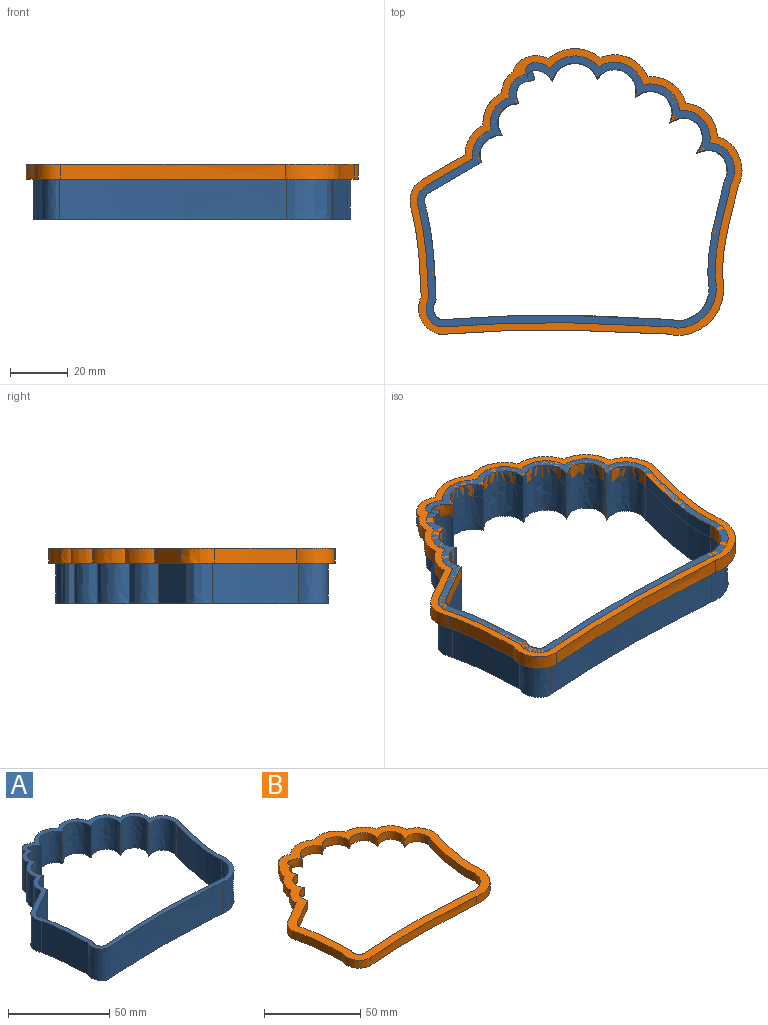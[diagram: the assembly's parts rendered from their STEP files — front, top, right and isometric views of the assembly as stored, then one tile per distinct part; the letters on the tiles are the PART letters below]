
ASSEMBLY  parts=2 mates=1
PART A: 36 faces, bbox 113.9x98.3x23.4 mm
  f0: plane 113.92x98.34mm, normal (0,0,1), area 899.7mm2, adj f2,f3,f4,f5,f6,f7,f8,f9
  f1: plane 113.92x98.34mm, normal (0,0,-1), area 899.7mm2, adj f2,f3,f4,f5,f6,f7,f8,f9
  f2: extruded ~19.05x1.86mm, area 34.7mm2, adj f0,f1,f15,f16
  f3: plane 19.05x16.29mm, normal (-0.5,0.87,0), area 358.4mm2, adj f0,f1,f4,f18
  f4: extruded ~19.05x9.03mm, area 192.8mm2, adj f0,f1,f3,f5
  f5: extruded ~29.67x19.05mm, area 569.3mm2, adj f0,f1,f4,f6
  f6: extruded ~19.05x9.98mm, area 258.5mm2, adj f0,f1,f5,f7
  f7: extruded ~78.37x19.05mm, area 1494.3mm2, adj f0,f1,f6,f8
  f8: extruded ~19.05x15.88mm, area 462.2mm2, adj f0,f1,f7,f9
  f9: extruded ~35.78x19.05mm, area 693.3mm2, adj f0,f1,f8,f10
  f10: extruded ~19.05x13.99mm, area 359.8mm2, adj f0,f1,f9,f11
  f11: extruded ~19.05x11.12mm, area 337.4mm2, adj f0,f1,f10,f12
  f12: extruded ~19.05x12.7mm, area 339.6mm2, adj f0,f1,f11,f13
  f13: extruded ~19.05x15.24mm, area 369.4mm2, adj f0,f1,f12,f14
  f14: extruded ~19.05x16.7mm, area 365mm2, adj f0,f1,f13,f15
  f15: extruded ~19.05x8.63mm, area 197.6mm2, adj f0,f1,f2,f14
  f16: extruded ~19.05x8.02mm, area 208.8mm2, adj f0,f1,f2,f17
  f17: extruded ~19.05x11.08mm, area 266.9mm2, adj f0,f1,f16,f18
  f18: extruded ~19.05x10.1mm, area 247.7mm2, adj f0,f1,f3,f17
  f19: plane 19.05x17.79mm, normal (0.5,-0.87,0), area 391.5mm2, adj f0,f1,f20,f35
  f20: extruded ~19.05x6.28mm, area 134.5mm2, adj f0,f1,f19,f21
  f21: extruded ~30.97x19.05mm, area 594.3mm2, adj f0,f1,f20,f22
  f22: extruded ~19.05x6.81mm, area 165.1mm2, adj f0,f1,f21,f23
  f23: extruded ~79.25x19.05mm, area 1511mm2, adj f0,f1,f22,f24
  f24: extruded ~19.05x12.78mm, area 372.4mm2, adj f0,f1,f23,f25
  f25: extruded ~37.02x19.05mm, area 717.1mm2, adj f0,f1,f24,f26
  f26: extruded ~19.05x10.79mm, area 356.3mm2, adj f0,f1,f25,f27
  f27: extruded ~19.05x12.22mm, area 416.6mm2, adj f0,f1,f26,f28
  f28: extruded ~19.05x12.71mm, area 405.8mm2, adj f0,f1,f27,f29
  f29: extruded ~19.05x13.49mm, area 400.9mm2, adj f0,f1,f28,f30
  f30: extruded ~19.05x15.52mm, area 397mm2, adj f0,f1,f29,f31
  f31: extruded ~19.05x6.71mm, area 158.1mm2, adj f0,f1,f30,f32
  f32: extruded ~19.05x3.64mm, area 103.9mm2, adj f0,f1,f31,f33
  f33: extruded ~19.05x7.71mm, area 190.2mm2, adj f0,f1,f32,f34
  f34: extruded ~19.05x10.91mm, area 299.5mm2, adj f0,f1,f33,f35
  f35: extruded ~19.05x9.39mm, area 269.4mm2, adj f0,f1,f19,f34
PART B: 36 faces, bbox 115.5x99.9x5.9 mm
  f0: plane 115.46x99.87mm, normal (0,0,1), area 1808.1mm2, adj f2,f3,f4,f5,f6,f7,f8,f9
  f1: plane 115.46x99.87mm, normal (0,0,-1), area 1808.1mm2, adj f2,f3,f4,f5,f6,f7,f8,f9
  f2: plane 15.1x8.73mm, normal (-0.5,0.87,0), area 88.6mm2, adj f0,f1,f3,f18
  f3: extruded ~11.77x5.08mm, area 66.8mm2, adj f0,f1,f2,f4
  f4: extruded ~28.47x5.08mm, area 145.7mm2, adj f0,f1,f3,f5
  f5: extruded ~13.05x8.86mm, area 93.2mm2, adj f0,f1,f4,f6
  f6: extruded ~77.6x5.08mm, area 394.6mm2, adj f0,f1,f5,f7
  f7: extruded ~18.9x16.93mm, area 147.2mm2, adj f0,f1,f6,f8
  f8: extruded ~34.62x5.37mm, area 178.8mm2, adj f0,f1,f7,f9
  f9: extruded ~17.09x8.48mm, area 107.3mm2, adj f0,f1,f8,f10
  f10: extruded ~11.51x10.91mm, area 88.4mm2, adj f0,f1,f9,f11
  f11: extruded ~13.12x9.23mm, area 88.3mm2, adj f0,f1,f10,f12
  f12: extruded ~16.54x7.6mm, area 100.4mm2, adj f0,f1,f11,f13
  f13: extruded ~17.68x5.08mm, area 98.2mm2, adj f0,f1,f12,f14
  f14: extruded ~7.66x5.08mm, area 40.3mm2, adj f0,f1,f13,f15
  f15: extruded ~5.08x4.76mm, area 35.1mm2, adj f0,f1,f14,f16
  f16: extruded ~7.37x5.08mm, area 44.2mm2, adj f0,f1,f15,f17
  f17: extruded ~11.26x6.45mm, area 69.8mm2, adj f0,f1,f16,f18
  f18: extruded ~10.19x6.2mm, area 63.7mm2, adj f0,f1,f2,f17
  f19: plane 17.79x10.29mm, normal (0.5,-0.87,0), area 104.4mm2, adj f0,f1,f20,f35
  f20: extruded ~6.28x5.08mm, area 35.9mm2, adj f0,f1,f19,f21
  f21: extruded ~30.97x5.08mm, area 158.5mm2, adj f0,f1,f20,f22
  f22: extruded ~6.81x5.08mm, area 44mm2, adj f0,f1,f21,f23
  f23: extruded ~79.25x5.08mm, area 402.9mm2, adj f0,f1,f22,f24
  f24: extruded ~12.78x11.48mm, area 99.3mm2, adj f0,f1,f23,f25
  f25: extruded ~37.02x5.72mm, area 191.2mm2, adj f0,f1,f24,f26
  f26: extruded ~10.79x10.4mm, area 95mm2, adj f0,f1,f25,f27
  f27: extruded ~12.22x11.45mm, area 111.1mm2, adj f0,f1,f26,f28
  f28: extruded ~12.71x11.07mm, area 108.2mm2, adj f0,f1,f27,f29
  f29: extruded ~13.49x9.61mm, area 106.9mm2, adj f0,f1,f28,f30
  f30: extruded ~15.52x6.16mm, area 105.9mm2, adj f0,f1,f29,f31
  f31: extruded ~6.71x5.08mm, area 41.9mm2, adj f0,f1,f30,f32
  f32: extruded ~5.08x3.64mm, area 24.2mm2, adj f0,f1,f31,f33
  f33: extruded ~7.71x5.08mm, area 50.7mm2, adj f0,f1,f32,f34
  f34: extruded ~10.91x7.34mm, area 79.9mm2, adj f0,f1,f33,f35
  f35: extruded ~9.39x7.73mm, area 71.9mm2, adj f0,f1,f19,f34
PLACE A t=(3.5,-6.36,-5.65)mm
PLACE B t=(-178.27,6.53,8.32)mm
MATE fastened A.f0 <-> B.f0  axis (0,0,1) through (-32.6,3.24,13.4)mm
